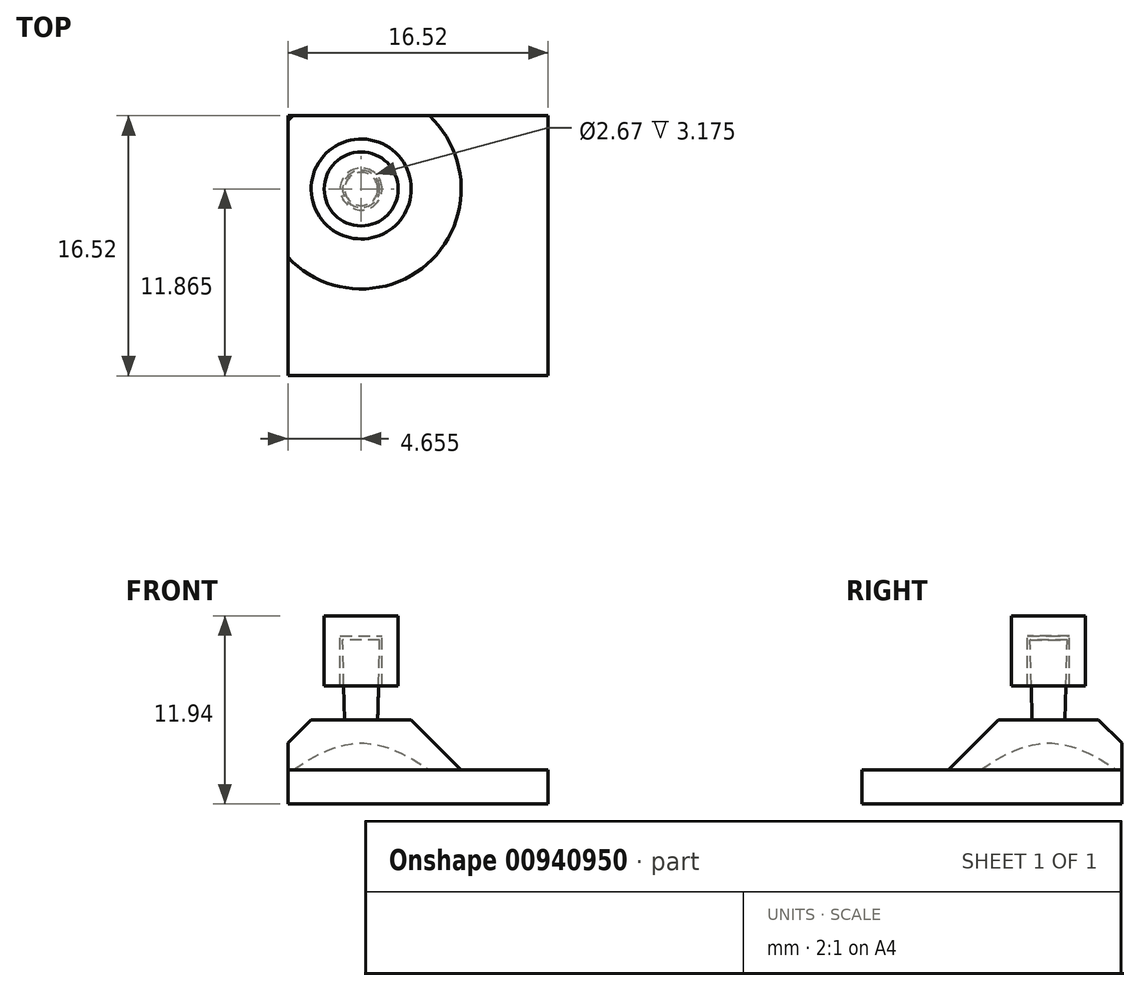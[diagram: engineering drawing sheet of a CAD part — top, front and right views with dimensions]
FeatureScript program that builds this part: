
annotation { "Feature Type Name" : "Feature", "Feature Type Description" : "" }
export const myFeature = defineFeature(function(context is Context, id is Id, definition is map)
    precondition{}
    {
        {
            var Q0;
            Q0=qCreatedBy(makeId("Top.planeOp"),FACE);
            var sketch = newSketch(context, id + "F0", { "sketchPlane" : qUnion([Q0])});
            skLineSegment(sketch, "E0.bottom", {"start": v(-8.25, 8.26) * mm, "end": v(8.25, 8.26) * mm});
            skLineSegment(sketch, "E0.top", {"start": v(-8.25, -8.26) * mm, "end": v(8.25, -8.26) * mm});
            skLineSegment(sketch, "E0.left", {"start": v(-8.26, 8.25) * mm, "end": v(-8.26, -8.25) * mm});
            skLineSegment(sketch, "E0.right", {"start": v(8.26, 8.25) * mm, "end": v(8.26, -8.25) * mm});
            skPoint(sketch, "E0.middle", {"position": v(0, 0) * mm});
            skSolve(sketch);
        }
        {
            var Q0;
            Q0 = qSketchRegion(id + "F0", true);
            extrude(context, id + "F1", {"entities" : qUnion([Q0]), "depth" : 2.16 * mm, "offsetDistance" : 25.4 * mm});
        }
        {
            var Q0;
            Q0=makeQuery(id+"F1.opExtrude","CAP_FACE",FACE,{"disambiguationData":[OSD([sQuery(id+"F0.wireOp",EDGE,"E0.bottom"),sQuery(id+"F0.wireOp",EDGE,"E0.top"),sQuery(id+"F0.wireOp",EDGE,"E0.left"),sQuery(id+"F0.wireOp",EDGE,"E0.right")])],"isStart":false});
            var sketch = newSketch(context, id + "F2", { "sketchPlane" : qUnion([Q0])});
            skCircle(sketch, "E1", {"center": v(-3.6, 3.6) * mm, "radius": 3.18 * mm});
            skLineSegment(sketch, "E2", {"start": v(-8.25, 8.26) * mm, "end": v(0, 0) * mm, "construction": true});
            skSolve(sketch);
        }
        {
            var Q0;
            Q0=makeQuery(id+"F2.imprint","IMPRINT",FACE,{"disambiguationData":[TD([[makeQuery(id+"F2.imprint","IMPRINT",EDGE,{"derivedFrom":sQuery(id+"F2.wireOp",EDGE,"E1")}),1.0]])]});
            extrude(context, id + "F3", {"entities" : qUnion([Q0]), "operationType" : NewBodyOperationType.ADD, "depth" : 3.17 * mm, "offsetDistance" : 25.4 * mm, "hasSecondDirection" : true, "secondDirectionOppositeDirection" : true, "secondDirectionDepth" : 1.27 * mm});
        }
        {
            var Q0;
            Q0=makeQuery(id+"F3.opExtrude","CAP_FACE",FACE,{"disambiguationData":[OSD([sQuery(id+"F2.wireOp",EDGE,"E1")])],"isStart":false});
            var sketch = newSketch(context, id + "F4", { "sketchPlane" : qUnion([Q0])});
            skCircle(sketch, "E3", {"center": v(-3.6, 3.6) * mm, "radius": 1.05 * mm});
            skSolve(sketch);
        }
        {
            var Q0;
            Q0 = qSketchRegion(id + "F4", true);
            extrude(context, id + "F5", {"entities" : qUnion([Q0]), "operationType" : NewBodyOperationType.ADD, "depth" : 5.08 * mm, "offsetDistance" : 25.4 * mm, "hasDraft" : true, "draftAngle" : 1.5 * degree});
        }
        {
            var Q0;
            Q0=makeQuery(id+"F5.opExtrude","CAP_FACE",FACE,{"disambiguationData":[OSD([sQuery(id+"F4.wireOp",EDGE,"E3")])],"isStart":false});
            var sketch = newSketch(context, id + "F6", { "sketchPlane" : qUnion([Q0])});
            skCircle(sketch, "E4", {"center": v(-3.6, 3.6) * mm, "radius": 1.18 * mm});
            skSolve(sketch);
        }
        {
            var Q0;
            Q0=makeQuery(id+"F6.imprint","IMPRINT",FACE,{"disambiguationData":[TD([[makeQuery(id+"F6.imprint","IMPRINT",EDGE,{"derivedFrom":sQuery(id+"F6.wireOp",EDGE,"E4")}),1.0]])]});
            cPlane(context, id + "F7", {"entities" : qUnion([Q0]), "cplaneType" : CPlaneType.OFFSET, "offset" : 0.25 * mm, "width" : 152.4 * mm, "height" : 152.4 * mm});
        }
        {
            var Q0;
            Q0=qCreatedBy(id+"F7.planeOp",FACE);
            var sketch = newSketch(context, id + "F8", { "sketchPlane" : qUnion([Q0])});
            skCircle(sketch, "E5", {"center": v(-3.6, 3.6) * mm, "radius": 2.35 * mm});
            skSolve(sketch);
        }
        {
            var Q0;
            Q0=makeQuery(id+"F8.imprint","IMPRINT",FACE,{"disambiguationData":[TD([[makeQuery(id+"F8.imprint","IMPRINT",EDGE,{"derivedFrom":sQuery(id+"F8.wireOp",EDGE,"E5")}),1.0]])]});
            extrude(context, id + "F9", {"entities" : qUnion([Q0]), "depth" : 1.27 * mm, "offsetDistance" : 25.4 * mm});
        }
        {
            var Q0;
            Q0=makeQuery(id+"F9.opExtrude","CAP_FACE",FACE,{"disambiguationData":[OSD([sQuery(id+"F8.wireOp",EDGE,"E5")])],"isStart":true});
            var sketch = newSketch(context, id + "F10", { "sketchPlane" : qUnion([Q0])});
            skCircle(sketch, "E6", {"center": v(-3.6, -3.6) * mm, "radius": 2.35 * mm});
            skCircle(sketch, "E7", {"center": v(-3.6, -3.6) * mm, "radius": 1.33 * mm});
            skSolve(sketch);
        }
        {
            var Q0;
            Q0 = qSketchRegion(id + "F10", true);
            extrude(context, id + "F11", {"entities" : qUnion([Q0]), "operationType" : NewBodyOperationType.ADD, "depth" : 3.17 * mm, "offsetDistance" : 25.4 * mm});
        }
        {
            var Q0;
            Q0=makeQuery(id+"F3.boolean.opBoolean","INTERSECT",EDGE,{"derivedFrom":[makeQuery(id+"F1.opExtrude","CAP_FACE",FACE,{"disambiguationData":[OSD([sQuery(id+"F0.wireOp",EDGE,"E0.bottom"),sQuery(id+"F0.wireOp",EDGE,"E0.top"),sQuery(id+"F0.wireOp",EDGE,"E0.left"),sQuery(id+"F0.wireOp",EDGE,"E0.right")])],"isStart":false}),makeQuery(id+"F3.opExtrude","SWEPT_FACE",FACE,{"disambiguationData":[OSD([sQuery(id+"F2.wireOp",EDGE,"E1")])]})]});
            chamfer(context, id + "F12", {"entities" : qUnion([Q0]), "width" : 3.17 * mm, "tangentPropagation" : true});
        }
    });
